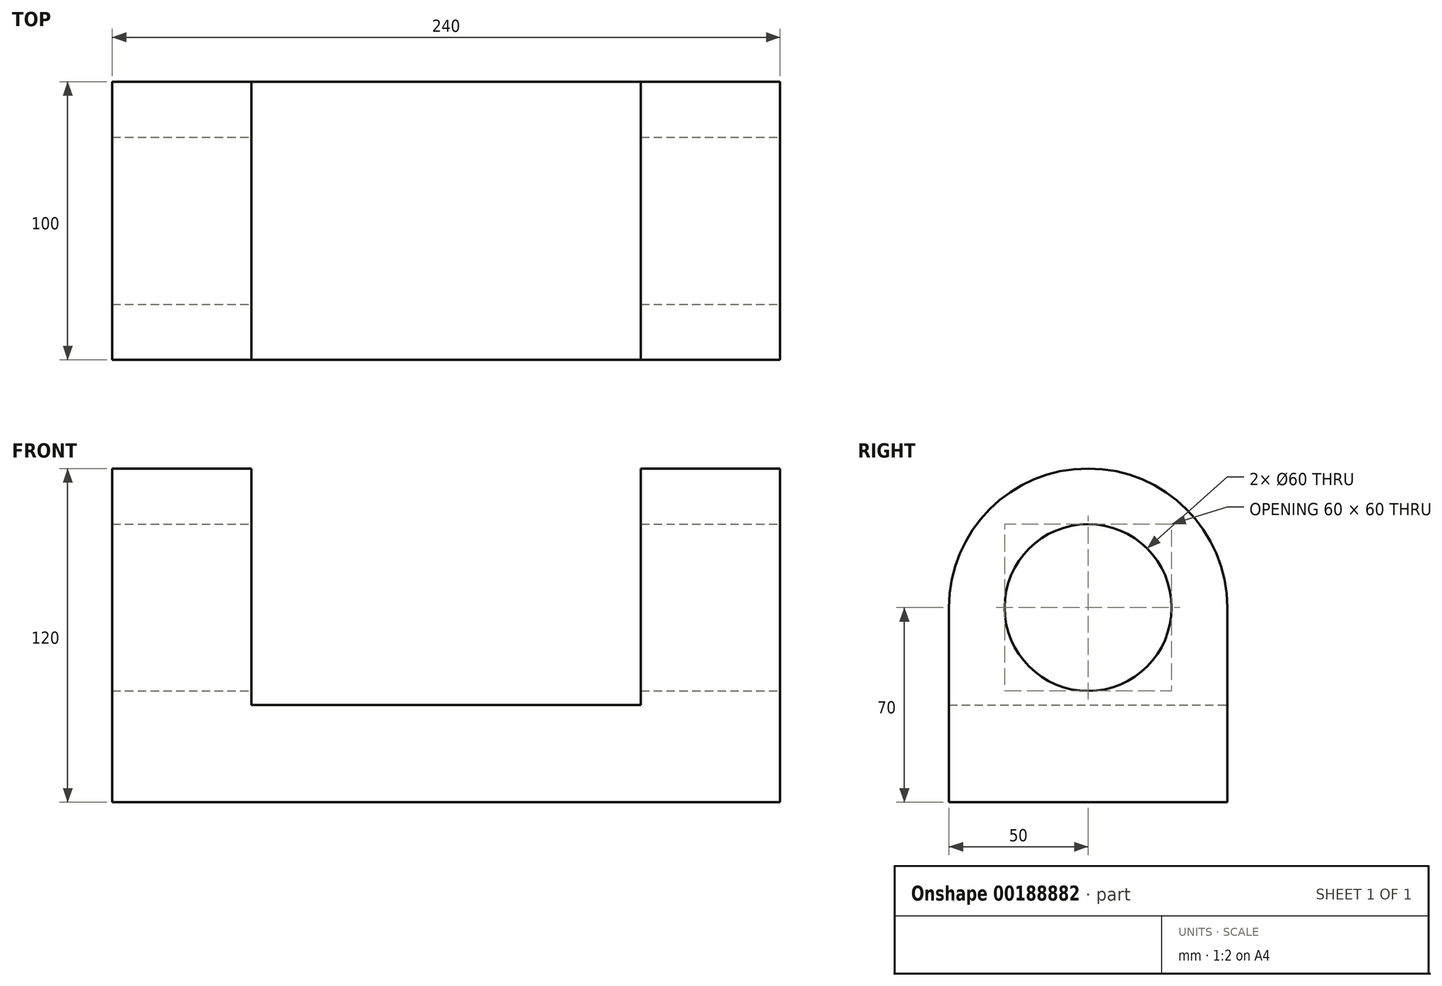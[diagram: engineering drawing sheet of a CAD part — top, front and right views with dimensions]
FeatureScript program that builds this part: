
annotation { "Feature Type Name" : "Feature", "Feature Type Description" : "" }
export const myFeature = defineFeature(function(context is Context, id is Id, definition is map)
    precondition{}
    {
        {
            var Q0;
            Q0=qCreatedBy(makeId("Right.planeOp"),FACE);
            var sketch = newSketch(context, id + "F0", { "sketchPlane" : qUnion([Q0])});
            skLineSegment(sketch, "E0", {"start": v(0, 0) * mm, "end": v(100, 0) * mm});
            skLineSegment(sketch, "E1", {"start": v(0, 0) * mm, "end": v(0, 70) * mm});
            skLineSegment(sketch, "E2", {"start": v(100, 0) * mm, "end": v(100, 70) * mm});
            skArc(sketch, "E3", {"start": v(0, 70) * mm, "mid": v(50, 120) * mm, "end": v(100, 70) * mm});
            skSolve(sketch);
        }
        {
            var Q0;
            Q0=qSketchRegion(id+"F0",true);
            extrude(context, id + "F1", {"entities" : qUnion([Q0]), "depth" : 240 * mm});
        }
        {
            var Q0;
            Q0=makeQuery(id+"F1.opExtrude","CAP_FACE",FACE,{"disambiguationData":[OSD([sQuery(id+"F0.wireOp",EDGE,"E0"),sQuery(id+"F0.wireOp",EDGE,"E1"),sQuery(id+"F0.wireOp",EDGE,"E2"),sQuery(id+"F0.wireOp",EDGE,"E3")])],"isStart":false});
            var sketch = newSketch(context, id + "F2", { "sketchPlane" : qUnion([Q0])});
            skCircle(sketch, "E4", {"center": v(50, 70) * mm, "radius": 30 * mm});
            skSolve(sketch);
        }
        {
            var Q0;
            Q0=qSketchRegion(id+"F2",true);
            extrude(context, id + "F3", {"entities" : qUnion([Q0]), "operationType" : NewBodyOperationType.REMOVE, "endBound" : BoundingType.UP_TO_NEXT, "oppositeDirection" : true, "depth" : 25 * mm});
        }
        {
            var Q0;
            Q0=makeQuery(id+"F1.opExtrude","SWEPT_FACE",FACE,{"disambiguationData":[OSD([sQuery(id+"F0.wireOp",EDGE,"E0")])]});
            cPlane(context, id + "F4", {"entities" : qUnion([Q0]), "cplaneType" : CPlaneType.OFFSET, "offset" : 35 * mm, "oppositeDirection" : true, "width" : 150 * mm, "height" : 150 * mm});
        }
        {
            var Q0;
            Q0=qCreatedBy(id+"F4.planeOp",FACE);
            var sketch = newSketch(context, id + "F5", { "sketchPlane" : qUnion([Q0])});
            skLineSegment(sketch, "E5.bottom", {"start": v(50, 0) * mm, "end": v(190, 0) * mm});
            skLineSegment(sketch, "E5.top", {"start": v(50, -100) * mm, "end": v(190, -100) * mm});
            skLineSegment(sketch, "E5.left", {"start": v(50, 0) * mm, "end": v(50, -100) * mm});
            skLineSegment(sketch, "E5.right", {"start": v(190, 0) * mm, "end": v(190, -100) * mm});
            skSolve(sketch);
        }
        {
            var Q0;
            Q0=qSketchRegion(id+"F5",true);
            extrude(context, id + "F6", {"entities" : qUnion([Q0]), "operationType" : NewBodyOperationType.REMOVE, "endBound" : BoundingType.THROUGH_ALL, "oppositeDirection" : true, "depth" : 25 * mm});
        }
    });
